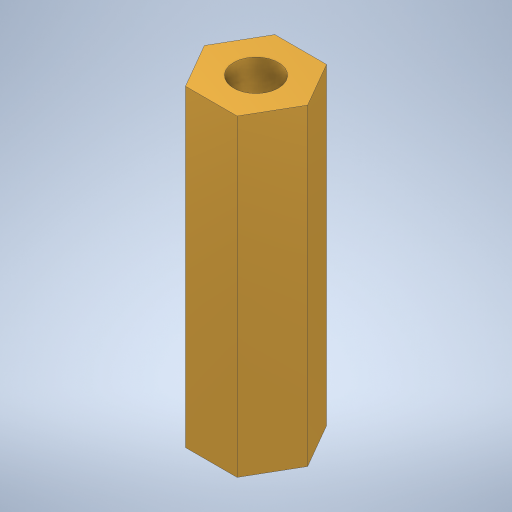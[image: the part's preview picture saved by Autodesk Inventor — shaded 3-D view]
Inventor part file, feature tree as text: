
AUTODESK INVENTOR PART (.ipt)
format: ipt  version: 2024.1 (Build 281209000, 209)  size: 232,448 bytes
history: native  units: mm
features: extrude x1, sketch x1
ambient origin geometry x8: Origin, YZ Plane, XZ Plane, XY Plane, X Axis, Y Axis, Z Axis, Center Point
bodies: Solide1 (feature_tree)
feature tree (2):
  extrude  "Extrusion1"  Depth=2.0mm
  sketch  "Esquisse1"
